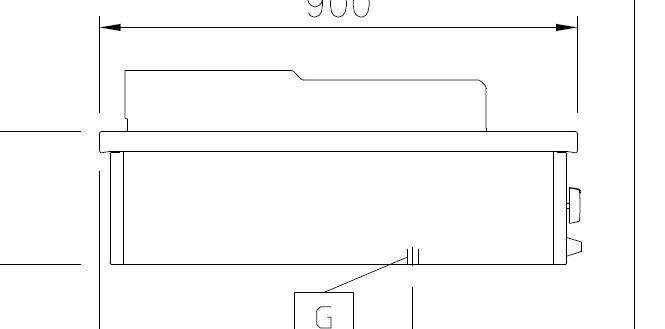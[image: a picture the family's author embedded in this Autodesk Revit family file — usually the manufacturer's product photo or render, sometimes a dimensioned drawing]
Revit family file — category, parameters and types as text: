
# Revit family: QF_ELECTROLUXPROFESSIONAL_589278_MCDAAADOPO
name_source: partatom
category: Specialty Equipment
revit_build: Autodesk Revit 2018 (Build: 20190510_1515(x64)
units: mm (PartAtom-declared; Revit-internal decimal feet)

## family parameters
Always vertical = Yes
Cut with Voids When Loaded = No
Part Type = Normal
Room Calculation Point = No
Round Connector Dimension = Use Diameter
Shared = No
Work Plane-Based = No

## types (1)
- QF_ELECTROLUXPROFESSIONAL_589278_MCDAAADOPO
    Description = GAS CHARGRILL,1-SIDE,400X900X250H
    Direct Waste Size = 0"
    Gas Connection Height = 0 mm  [stored 0 ft]
    Gas KW = 10.5
    Gas Size = 1"
    HP = 0 HP
    Manufacturer = ELECTROLUX
    Model = 589278
    Watts = 0 W
    Weight in Pounds = 143.3

note: [stored X ft] marks values corroborated as IEEE doubles in the binary element streams (Revit-internal decimal feet)

## geometry (parser evidence)
native form markers: Blend x28, Sweep x10
no freeform markers — native parametric forms only
